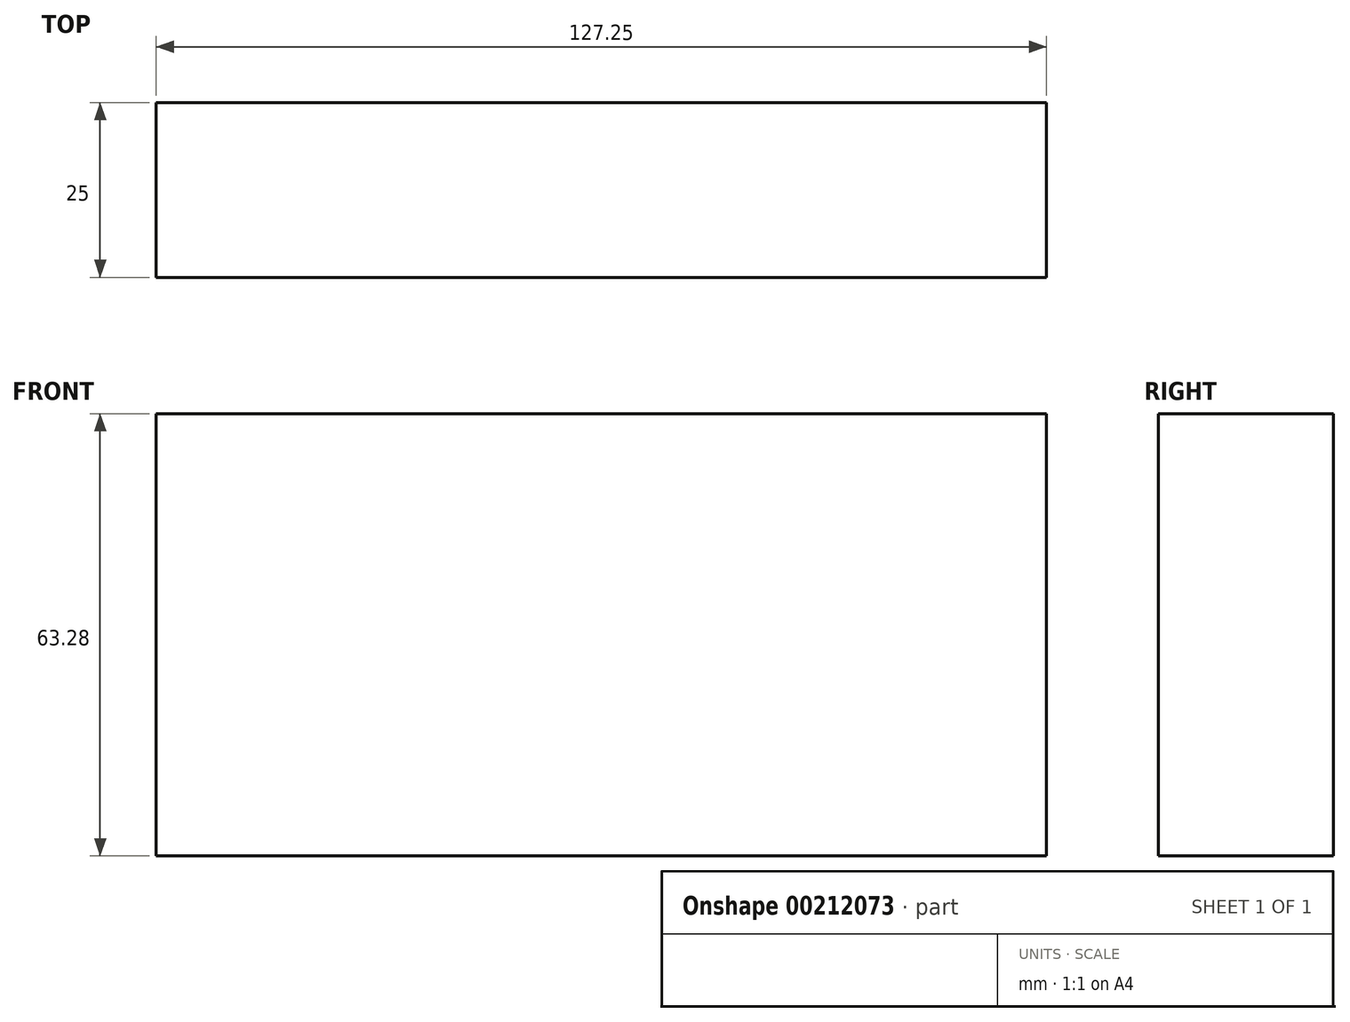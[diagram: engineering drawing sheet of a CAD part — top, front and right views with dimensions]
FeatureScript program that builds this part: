
annotation { "Feature Type Name" : "Feature", "Feature Type Description" : "" }
export const myFeature = defineFeature(function(context is Context, id is Id, definition is map)
    precondition{}
    {
        {
            var Q0;
            Q0=qCreatedBy(makeId("Front.planeOp"),FACE);
            var sketch = newSketch(context, id + "F0", { "sketchPlane" : qUnion([Q0])});
            skLineSegment(sketch, "E0.bottom", {"start": v(-31.42, 18.16) * mm, "end": v(95.83, 18.16) * mm});
            skLineSegment(sketch, "E0.top", {"start": v(-31.42, -45.12) * mm, "end": v(95.83, -45.12) * mm});
            skLineSegment(sketch, "E0.left", {"start": v(-31.42, 18.16) * mm, "end": v(-31.42, -45.12) * mm});
            skLineSegment(sketch, "E0.right", {"start": v(95.83, 18.16) * mm, "end": v(95.83, -45.12) * mm});
            skSolve(sketch);
        }
        {
            var Q0;
            Q0=makeQuery(id+"F0.imprint","IMPRINT",FACE,{"disambiguationData":[TD([[makeQuery(id+"F0.imprint","IMPRINT",EDGE,{"derivedFrom":sQuery(id+"F0.wireOp",EDGE,"E0.bottom")}),-1.0]])]});
            extrude(context, id + "F1", {"entities" : qUnion([Q0]), "depth" : 25 * mm});
        }
    });
